# Revit family: Plumbing-Faucet-Sloan-Valve-EBF-825
name_source: partatom
category: Plumbing Fixtures
units: mm (PartAtom-declared; Revit-internal decimal feet)

## family parameters
Cut with Voids When Loaded = No
Host = Face
OmniClass Number = 23.45.55.14
OmniClass Title = Single Faucets
Part Type = Normal
Room Calculation Point = No
Round Connector Dimension = Use Diameter
Shared = No

## types (16) — shared parameters
Assembly Code = D2010
CW Connection = Yes
CWFU = 1.5
Default Elevation = 0"
Depth = 8 3/8"
Edition number = 1
HW Connection = Yes
HWFU = 1.5
Height = 2 7/8"
Keynote = 15410
Manufacturer = Sloan Valve
URL = www.sloanvalve.com
Valve Pressure Drop = 0.00 psi
Vent Connection = No
Waste Connection = No
Water Inlet Connection Description = Pretempered Water Supply Connection
Water Inlet Connection Diameter = 0"
Width = 2 7/8"
zero-valued in all types: WFU

## per-type parameters (varying)
| type | Description | Part Number | Product Material | Water Flow |
| EBF-825-BAT-BDM-CP-0.35GPM-MLM-IR-FCT | Battery Power Supply, Below Deck Manual Mixing Valve, Polished Chrome Finish, 0.35 gpm, Multi-Laminar Spray, Infrared Sensor, Optima® Battery-Powered Wall-Mounted Wall Body. | 3315449BT | Sloan Valve - Finish - Polished Chrome | 0 GPM |
| EBF-825-BAT-BDM-CP-0.5GPM-MLM-IR-FCT | Battery Power Supply, Below Deck Manual Mixing Valve, Polished Chrome Finish, 0.5 gpm, Multi-Laminar Spray, Infrared Sensor, Optima® Battery-Powered Wall-Mounted Wall Body. | 3315456BT | Sloan Valve - Finish - Polished Chrome | 1 GPM |
| EBF-825-BAT-BDT-CP-0.35GPM-MLM-IR-FCT | Battery Power Supply, Below Deck Thermostatic Mixing Valve, Polished Chrome Finish, 0.35 gpm, Multi-Laminar Spray, Infrared Sensor, Optima® Battery-Powered Wall-Mounted Wall Body. | 3315450BT | Sloan Valve - Finish - Polished Chrome | 0 GPM |
| EBF-825-BAT-BDT-CP-0.5GPM-MLM-IR-FCT | Battery Power Supply, Below Deck Thermostatic Mixing Valve, Polished Chrome Finish, 0.5 gpm, Multi-Laminar Spray, Infrared Sensor, Optima® Battery-Powered Wall-Mounted Wall Body. | 3315457BT | Sloan Valve - Finish - Polished Chrome | 1 GPM |
| EBF-825-BAT-TEE-CP-0.35GPM-MLM-IR-FCT | Battery Power Supply, Back-Check Tee, Polished Chrome Finish, 0.35 gpm, Multi-Laminar Spray, Infrared Sensor, Optima® Battery-Powered Wall-Mounted Wall Body. | 3315451BT | Sloan Valve - Finish - Polished Chrome | 0 GPM |
| EBF-825-BAT-TEE-CP-0.5GPM-MLM-IR-FCT | Battery Power Supply, Back-Check Tee, Polished Chrome Finish, 0.5 gpm, Multi-Laminar Spray, Infrared Sensor, Optima® Battery-Powered Wall-Mounted Wall Body. | 3315458BT | Sloan Valve - Finish - Polished Chrome | 1 GPM |
| EBF-825-BAT-TEE-BN-0.5GPM-MLM-IR-FCT | Battery Power Supply, Back-Check Tee, Brushed Nickel Finish, 0.5 gpm, Multi-Laminar Spray, Infrared Sensor, Optima® Battery-Powered Wall-Mounted Wall Body. | 3315455BT | Sloan Valve - Finish - Brushed Nickel | 1 GPM |
| EBF-825-TUR-BDM-CP-0.35GPM-MLM-IR-FCT | Battery + Turbine Power Supply, Below Deck Manual Mixing Valve, Polished Chrome Finish, 0.35 gpm, Multi-Laminar Spray, Infrared Sensor, Optima® Battery-Powered Wall-Mounted Wall Body. | 3315452BT | Sloan Valve - Finish - Polished Chrome | 0 GPM |
| EBF-825-TUR-BDM-CP-0.5GPM-MLM-IR-FCT | Battery + Turbine Power Supply, Below Deck Manual Mixing Valve, Polished Chrome Finish, 0.5 gpm, Multi-Laminar Spray, Infrared Sensor, Optima® Battery-Powered Wall-Mounted Wall Body. | 3315459BT | Sloan Valve - Finish - Polished Chrome | 1 GPM |
| EBF-825-BAT-TEE-GR-0.5GPM-MLM-IR-FCT | Battery Power Supply, Back-Check Tee, Graphite Finish, 0.5 gpm, Multi-Laminar Spray, Infrared Sensor, Optima® Battery-Powered WallMounted Wall Body. | 3315462BT | Sloan Valve - Finish - Graphite | 1 GPM |
| EBF-825-BAT-TEE-PB-0.5GPM-MLM-IR-FCT | Battery Power Supply, Back-Check Tee, Polished Brass Finish, 0.5 gpm, Multi-Laminar Spray, Infrared Sensor, Optima® Battery-Powered Wall-Mounted Wall Body. | 3315463BT | Sloan Valve - Finish - Polished Brass | 1 GPM |
| EBF-825-BAT-TEE-SF-0.5GPM-MLM-IR-FCT | Battery Power Supply, Back-Check Tee, Brushed Stainless Finish, 0.5 gpm, Multi-Laminar Spray, Infrared Sensor, Optima® Battery-Powered Wall-Mounted Wall Body. | 3315464BT | Sloan Valve - Finish - Brushed Stainless Steel | 1 GPM |
| EBF-825-TUR-BDT-CP-0.35GPM-MLM-IR-FCT | Battery + Turbine Power Supply, Below Deck Thermostatic Mixing Valve, Polished Chrome Finish, 0.35 gpm, Multi-Laminar Spray, Infrared Sensor, Optima® Battery-Powered Wall-Mounted Wall Body. | 3315453BT | Sloan Valve - Finish - Polished Chrome | 0 GPM |
| EBF-825-TUR-BDT-CP-0.5GPM-MLM-IR-FCT | Battery + Turbine Power Supply, Below Deck Thermostatic Mixing Valve, Polished Chrome Finish, 0.5 gpm, Multi-Laminar Spray, Infrared Sensor, Optima® Battery-Powered Wall-Mounted Wall Body. | 3315460BT | Sloan Valve - Finish - Polished Chrome | 1 GPM |
| EBF-825-TUR-TEE-CP-0.35GPM-MLM-IR-FCT | Battery + Turbine Power Supply, Back-Check Tee, Polished Chrome Finish, 0.35 gpm, Multi-Laminar Spray, Infrared Sensor, Optima® Battery-Powered Wall-Mounted Wall Body. | 3315454BT | Sloan Valve - Finish - Polished Chrome | 0 GPM |
| EBF-825-TUR-TEE-CP-0.5GPM-MLM-IR-FCT | Battery + Turbine Power Supply, Back-Check Tee, Polished Chrome Finish, 0.5 gpm, Multi-Laminar Spray, Infrared Sensor, Optima® Battery-Powered Wall-Mounted Wall Body. | 3315461BT | Sloan Valve - Finish - Polished Chrome | 1 GPM |

note: column(s) folded — value = type name in every type: Model

## geometry (parser evidence)
native form markers: Sweep x9
no freeform markers — native parametric forms only
